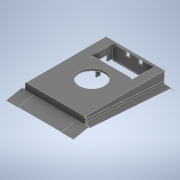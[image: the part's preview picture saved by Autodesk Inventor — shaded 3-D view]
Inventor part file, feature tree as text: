
AUTODESK INVENTOR PART (.ipt)
format: ipt  version: 2022 (Build 260153000, 153)  size: 934,912 bytes
history: native  units: mm
features: sketch x39, extrude x38, chamfer x4, mirror x2, fillet x1
ambient origin geometry x8: Origin, YZ Plane, XZ Plane, XY Plane, X Axis, Y Axis, Z Axis, Center Point
bodies: Solid1 (feature_tree)
feature tree (84):
  extrude  "Extrusion1"  Depth=140.0mm
  extrude  "Extrusion2"  Depth=2.5mm
  extrude  "Extrusion3"  Depth=3.2mm
  extrude  "Extrusion4"  Depth=37.867531mm
  extrude  "Extrusion5"  Depth=1.5mm
  extrude  "Extrusion6"  Depth=2.5mm
  extrude  "Extrusion7"  TaperAngle=0.0deg  [1 undecoded]
  extrude  "Extrusion8"  Depth=100.0mm
  extrude  "Extrusion9"  Depth=1.0mm
  extrude  "Extrusion10"  Depth=16.0mm TaperAngle=0.0deg
  extrude  "Extrusion11"  Depth=1.0mm
  extrude  "Extrusion12"  TaperAngle=0.0deg  [1 undecoded]
  fillet  "Fillet1"  Radius=12.0mm
  chamfer  "Chamfer1"  [1 undecoded]
  extrude  "Extrusion14"  Depth=100.0mm
  extrude  "Extrusion15"  Depth=0.2mm
  sketch  "Sketch23"  dims[d39=27.8mm d40=2.45mm d41=0.0mm d42=0.0mm]
  extrude  "Extrusion16"  Depth=0.5mm
  chamfer  "Chamfer2"  Distance=32.0mm
  extrude  "Extrusion17"  Depth=3.0mm TaperAngle=0.0deg
  extrude  "Extrusion18"  Depth=11.0mm TaperAngle=45.0deg
  extrude  "Extrusion19"  TaperAngle=0.0deg  [1 undecoded]
  extrude  "Extrusion20"  Depth=11.0mm TaperAngle=45.0deg
  extrude  "Extrusion21"  Depth=1.5mm
  sketch  "Sketch32"  dims[d50=105.0deg]
  extrude  "Extrusion22"  Depth=20.0mm
  extrude  "Extrusion23"  Depth=6.0mm TaperAngle=0.0deg
  extrude  "Extrusion24"  Depth=0.5mm TaperAngle=0.0deg
  extrude  "Extrusion25"  Depth=2.0mm TaperAngle=0.0deg
  extrude  "Extrusion26"  Depth=1.0mm
  extrude  "Extrusion27"  Depth=22.2mm TaperAngle=0.0deg
  chamfer  "Chamfer3"  Distance=20.0mm
  chamfer  "Chamfer4"  Distance=86.25mm
  extrude  "Extrusion28"  Depth=2.0mm TaperAngle=0.0deg
  mirror  "Mirror1"
  extrude  "Extrusion29"  Depth=20.0mm
  extrude  "Extrusion30"  Depth=0.2mm
  extrude  "Extrusion31"  Depth=20.0mm
  extrude  "Extrusion32"  Depth=5.0mm TaperAngle=0.0deg
  extrude  "Extrusion33"  Depth=67.0mm
  extrude  "Extrusion34"  Depth=8.0mm
  extrude  "Extrusion35"  Depth=2.5mm TaperAngle=0.0deg
  extrude  "Extrusion36"  Depth=5.0mm
  extrude  "Extrusion37"  Depth=5.0mm TaperAngle=0.0deg
  mirror  "Mirror4"
  extrude  "Extrusion38"  Depth=11.5mm
  extrude  "Extrusion39"  Depth=3.0mm TaperAngle=0.0deg
  sketch  "Sketch1"  dims[d0=212.0143mm d1=140.0mm]
  sketch  "Sketch2"  dims[d2=2.5mm d3=0.0mm d5=6.45mm]
  sketch  "Sketch3"  dims[d6=40.4609mm d7=0.0mm d8=3.2mm]
  sketch  "Sketch4"  dims[d9=15.009832mm d10=37.867531mm]
  sketch  "Sketch5"  dims[d11=37.96mm d12=1.5mm]
  sketch  "Sketch7"  dims[d14=2.5mm d15=17.453293mm]
  sketch  "Sketch8"  dims[d17=2.5mm d18=0.0mm d19=0.0mm]
  sketch  "Sketch9"  dims[d20=50.0mm d21=100.0mm]
  sketch  "Sketch11"  dims[d23=8.0mm d24=1.0mm]
  sketch  "Sketch12"  dims[d25=17.28mm d26=16.0mm d27=0.0mm]
  sketch  "Sketch13"  dims[d28=1.0mm d30=1.0mm]
  sketch  "Sketch14"  dims[d31=3.0mm d32=0.0mm d33=0.0mm d35=12.0mm d36=0.0mm]
  sketch  "Sketch17"  dims[d37=2.5mm]
  sketch  "Sketch20"  dims[d38=41.8054mm]
  sketch  "Sketch24"  dims[d43=16.406095mm]
  sketch  "Sketch26"  dims[d44=16.89mm]
  sketch  "Sketch27"  dims[d45=17.5mm]
  sketch  "Sketch29"  dims[d46=16.406095mm]
  sketch  "Sketch30"  dims[d47=105.0deg]
  sketch  "Sketch31"  dims[d49=7.15mm]
  sketch  "Sketch33"  dims[d51=6.0mm]
  sketch  "Sketch34"  dims[d52=25.4221mm]
  sketch  "Sketch35"  dims[d56=5.0mm]
  sketch  "Sketch36"  dims[d57=2.3435mm]
  sketch  "Sketch37"  dims[d58=16.231562mm]
  sketch  "Sketch39"  dims[d59=1.5mm]
  sketch  "Sketch40"  dims[d60=9.6051mm d61=0.0mm d62=0.0mm]
  sketch  "Sketch41"  dims[d65=50.0mm d66=100.0mm]
  sketch  "Sketch42"  dims[d67=0.0mm d68=0.0mm d69=0.2mm]
  sketch  "Sketch43"  dims[d70=0.5mm d71=2.55mm]
  sketch  "Sketch44"  dims[d72=0.5mm]
  sketch  "Sketch45"  dims[d73=0.5mm]
  sketch  "Sketch47"  dims[d74=0.8mm d75=32.0mm d76=0.0mm]
  sketch  "Sketch48"  dims[d77=12.0mm d78=0.0mm d79=3.0mm d80=0.0mm]
  sketch  "Sketch49"  dims[d81=1.5mm d85=8.5mm d86=11.0mm d87=45.0deg]
  sketch  "Sketch51"  dims[d88=12.0mm d89=0.0mm d90=0.0mm d91=0.0mm]
  sketch  "Sketch52"  dims[d92=10.0mm d93=0.0mm d94=0.395mm d95=11.0mm d96=45.0deg d97=1.5mm d98=0.8mm d99=6.0mm d100=0.0mm d101=0.5mm d102=2.5mm d103=0.0mm d104=0.0mm d105=40.0mm d106=2.0mm d107=0.0mm d108=0.0mm d109=1.0mm d110=22.2mm d111=0.0mm d112=20.0mm d113=0.0mm d114=86.25mm d115=2.0mm d116=0.0mm d117=16.4392mm d118=0.2mm d119=82.2292mm d121=5.0mm d122=0.0mm d125=67.0mm d126=8.0mm d127=2.5mm d128=0.0mm d129=5.0mm d130=5.0mm d131=0.0mm d132=11.5mm d133=3.0mm d134=0.0mm d135=10.5mm d136=10.5mm d137=0.0mm d138=10.5mm d139=10.5mm d140=45.0deg d141=10.5mm d142=10.5mm d143=45.0deg d144=0.0mm d145=0.0mm d146=4.0mm d147=5.0mm d148=4.0mm d149=56.8mm d150=18.5mm d151=1.5mm d152=1.5mm d153=10.0mm d154=0.0mm d155=35.0mm d156=35.0mm d157=0.0mm d158=0.0mm d159=7.5mm d160=0.0mm d161=7.5mm d162=5.0mm d163=0.0mm d164=5.0mm d165=0.0mm d166=3.0mm d167=0.0mm d168=8.5mm d169=3.0mm d170=0.0mm d171=4.0mm d172=8.0mm d173=0.0mm d174=6.0mm d175=5.0mm d176=2.0mm d177=0.0mm d181=24.0mm d182=2.0mm d183=20.0mm d184=12.0mm d185=0.0mm d186=0.0mm d187=5.0mm d188=12.0mm d189=10.0mm d190=10.0mm d191=20.0mm d192=0.0mm]
note: 4 required parameter values undecoded (feature->parameter linkage not recoverable at this tier; creation-order binding heuristic only, values carry confidence <= 0.55)
